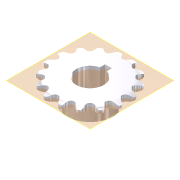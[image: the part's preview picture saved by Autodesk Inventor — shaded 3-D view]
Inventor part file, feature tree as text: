
AUTODESK INVENTOR PART (.ipt)
format: ipt  version: 2011 (Build 150239000, 239)  size: 524,288 bytes
history: native  units: mm
features: other x10, extrude x4, sketch x3, pattern_linear x1, pattern_circular x1, reference x1
ambient origin geometry x8: Origin, YZ Plane, XZ Plane, XY Plane, X Axis, Y Axis, Z Axis, Center Point
bodies: Solid1 (feature_tree)
feature tree (20):
  other  "25 sprocket 16T 500Key"
  other  "Blocks"
  other  "Theoretical Tooth Profile"
  other  "Tooth Profile"
  other  "Section Profile"
  other  "Shroud"
  other  "Strand"
  pattern_linear  "Strand Pattern"  Spacing1=22.471114mm  [1 undecoded]
  extrude  "Theoretical Tooth"  Depth=2.530727mm
  extrude  "Tooth"  Depth=2.64mm
  pattern_circular  "Tooth Pattern"  [2 undecoded]
  other  "Timing Plane"
  extrude  "Extrusion4"  Depth=4.62mm
  extrude  "Extrusion5"  Depth=10.0mm TaperAngle=0.0deg
  sketch  "Sketch6"  dims[d3=1.6665mm d10=22.471114mm d11=2.530727mm d12=2.64mm d13=4.3065mm d14=4.62mm d18=10.0mm d19=0.0mm d20=160.0mm d21=360.0deg d23=1.905mm d28=0.0mm d29=0.0mm d30=2.883mm d31=17.554806mm d32=2.883mm d33=0.8255mm d34=6.35mm d36=90.0deg d37=90.0deg d38=10.0mm d40=6.4mm d42=0.0mm d43=1.4415mm d44=23.452862mm d45=1.6665mm d46=7.128mm d47=0.0mm d48=25.4mm d49=0.0mm d50=10.0mm d51=21.59mm d52=7.493mm d53=0.0mm d54=12.7508mm d55=3.175mm d56=2.38125mm d57=7.493mm d58=0.0mm]
  sketch  "Sketch4"  dims[d0=32.549026mm]
  sketch  "Sketch5"  dims[d2=22.5deg]
  other  "500Key"
  reference  "Reference1"
  other  "500Key:1"
note: 3 required parameter values undecoded (feature->parameter linkage not recoverable at this tier; creation-order binding heuristic only, values carry confidence <= 0.55)
